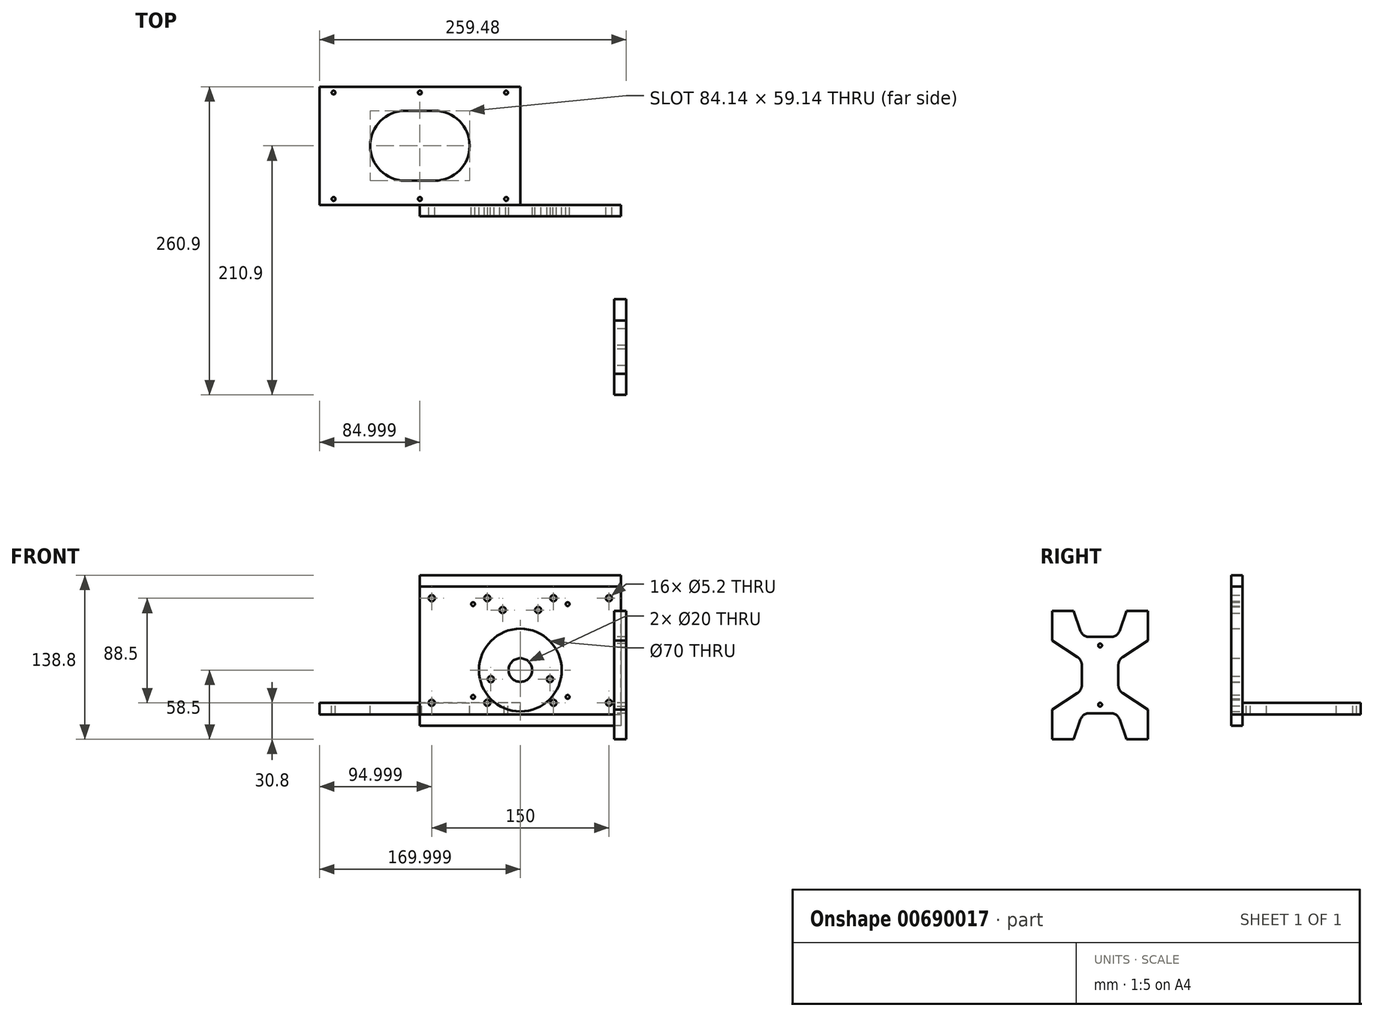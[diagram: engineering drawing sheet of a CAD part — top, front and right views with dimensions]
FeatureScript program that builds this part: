
annotation { "Feature Type Name" : "Feature", "Feature Type Description" : "" }
export const myFeature = defineFeature(function(context is Context, id is Id, definition is map)
    precondition{}
    {
        {
            var Q0;
            Q0=qCreatedBy(makeId("Front.planeOp"),FACE);
            var sketch = newSketch(context, id + "F0", { "sketchPlane" : qUnion([Q0])});
            skLineSegment(sketch, "E0.bottom", {"start": v(-124.48, -10) * mm, "end": v(-34.48, -10) * mm});
            skLineSegment(sketch, "E0.top", {"start": v(-124.48, 98.5) * mm, "end": v(-34.48, 98.5) * mm});
            skLineSegment(sketch, "E0.left", {"start": v(-124.48, -10) * mm, "end": v(-124.48, 98.5) * mm});
            skLineSegment(sketch, "E0.right", {"start": v(-34.48, -10) * mm, "end": v(-34.48, 98.5) * mm});
            skLineSegment(sketch, "E1", {"start": v(-114.8, 27.7) * mm, "end": v(-55.3, 27.7) * mm, "construction": true});
            skCircle(sketch, "E2", {"center": v(-79.48, 27.7) * mm, "radius": 10 * mm});
            skLineSegment(sketch, "E3", {"start": v(-104.48, 103.79) * mm, "end": v(-104.48, -19.33) * mm, "construction": true});
            skLineSegment(sketch, "E4", {"start": v(-94.48, 107.47) * mm, "end": v(-94.48, -17.72) * mm, "construction": true});
            skLineSegment(sketch, "E5", {"start": v(-64.48, 105.92) * mm, "end": v(-64.48, -18.24) * mm, "construction": true});
            skLineSegment(sketch, "E6", {"start": v(-54.48, 104.54) * mm, "end": v(-54.48, -18.06) * mm, "construction": true});
            skLineSegment(sketch, "E7", {"start": v(-24.43, 78.5) * mm, "end": v(-130.75, 78.5) * mm, "construction": true});
            skLineSegment(sketch, "E8", {"start": v(-125.67, 20) * mm, "end": v(-19.96, 20) * mm, "construction": true});
            skCircle(sketch, "E9", {"center": v(-94.48, 78.5) * mm, "radius": 2.6 * mm});
            skCircle(sketch, "E10", {"center": v(-64.48, 78.5) * mm, "radius": 2.6 * mm});
            skCircle(sketch, "E11", {"center": v(-54.48, 20) * mm, "radius": 2.6 * mm});
            skCircle(sketch, "E12", {"center": v(-104.48, 20) * mm, "radius": 2.6 * mm});
            skCircle(sketch, "E13", {"center": v(-79.48, 27.7) * mm, "radius": 35 * mm});
            skLineSegment(sketch, "E14.bottom", {"start": v(-124.48, -10) * mm, "end": v(-164.48, -10) * mm});
            skLineSegment(sketch, "E14.top", {"start": v(-124.48, 98.5) * mm, "end": v(-164.48, 98.5) * mm});
            skLineSegment(sketch, "E14.right", {"start": v(-164.48, -10) * mm, "end": v(-164.48, 98.5) * mm});
            skLineSegment(sketch, "E15.bottom", {"start": v(-34.48, -10) * mm, "end": v(5.52, -10) * mm});
            skLineSegment(sketch, "E15.top", {"start": v(-34.48, 98.5) * mm, "end": v(5.52, 98.5) * mm});
            skLineSegment(sketch, "E15.right", {"start": v(5.52, -10) * mm, "end": v(5.52, 98.5) * mm});
            skCircle(sketch, "E16", {"center": v(-107.48, 0) * mm, "radius": 2.6 * mm});
            skCircle(sketch, "E17", {"center": v(-51.48, 0) * mm, "radius": 2.6 * mm});
            skCircle(sketch, "E18", {"center": v(-51.48, 88.5) * mm, "radius": 2.6 * mm});
            skCircle(sketch, "E19", {"center": v(-107.48, 88.5) * mm, "radius": 2.6 * mm});
            skLineSegment(sketch, "E20", {"start": v(-191.34, 0) * mm, "end": v(90.56, 0) * mm, "construction": true});
            skLineSegment(sketch, "E21", {"start": v(-191.67, 88.5) * mm, "end": v(79.33, 88.5) * mm, "construction": true});
            skLineSegment(sketch, "E22", {"start": v(-107.48, -48.79) * mm, "end": v(-107.48, 164.35) * mm, "construction": true});
            skLineSegment(sketch, "E23", {"start": v(-51.48, -54.74) * mm, "end": v(-51.48, 152.44) * mm, "construction": true});
            skCircle(sketch, "E24", {"center": v(-154.44, 88.5) * mm, "radius": 2.6 * mm});
            skCircle(sketch, "E25", {"center": v(-4.48, 88.5) * mm, "radius": 2.6 * mm});
            skCircle(sketch, "E26", {"center": v(-4.48, 0) * mm, "radius": 2.6 * mm});
            skLineSegment(sketch, "E27", {"start": v(-4.48, 123.23) * mm, "end": v(-4.48, -81.76) * mm, "construction": true});
            skLineSegment(sketch, "E28", {"start": v(-154.48, 116.5) * mm, "end": v(-154.48, -51.97) * mm, "construction": true});
            skCircle(sketch, "E29", {"center": v(-154.48, 0) * mm, "radius": 2.6 * mm});
            skLineSegment(sketch, "E30", {"start": v(-119.48, 133.53) * mm, "end": v(-119.48, -72.31) * mm, "construction": true});
            skLineSegment(sketch, "E31", {"start": v(-39.48, 143.72) * mm, "end": v(-39.48, -75.85) * mm, "construction": true});
            skLineSegment(sketch, "E32", {"start": v(-190.12, 83.5) * mm, "end": v(57.15, 83.5) * mm, "construction": true});
            skLineSegment(sketch, "E33", {"start": v(-180.8, 5) * mm, "end": v(49.63, 5) * mm, "construction": true});
            skCircle(sketch, "E34", {"center": v(-119.48, 83.5) * mm, "radius": 1.6 * mm});
            skCircle(sketch, "E35", {"center": v(-39.48, 83.5) * mm, "radius": 1.6 * mm});
            skCircle(sketch, "E36", {"center": v(-39.48, 5) * mm, "radius": 1.6 * mm});
            skCircle(sketch, "E37", {"center": v(-119.48, 5) * mm, "radius": 1.6 * mm});
            skLineSegment(sketch, "E38", {"start": v(5.52, 98.5) * mm, "end": v(5.52, 108) * mm});
            skLineSegment(sketch, "E39", {"start": v(5.52, 108) * mm, "end": v(-164.48, 108) * mm});
            skLineSegment(sketch, "E40", {"start": v(-164.48, 108) * mm, "end": v(-164.48, 98.5) * mm});
            skLineSegment(sketch, "E41", {"start": v(5.52, -10) * mm, "end": v(5.52, -19.5) * mm});
            skLineSegment(sketch, "E42", {"start": v(5.52, -19.5) * mm, "end": v(-164.48, -19.5) * mm});
            skLineSegment(sketch, "E43", {"start": v(-164.48, -19.5) * mm, "end": v(-164.48, -10) * mm});
            skSolve(sketch);
        }
        {
            var Q0;
            Q0=makeQuery(id+"F0.imprint","IMPRINT",FACE,{"disambiguationData":[TD([[makeQuery(id+"F0.imprint","IMPRINT",EDGE,{"derivedFrom":sQuery(id+"F0.wireOp",EDGE,"E0.bottom")}),1.0]])]});
            var Q1;
            Q1=makeQuery(id+"F0.imprint","IMPRINT",FACE,{"disambiguationData":[TD([[makeQuery(id+"F0.imprint","IMPRINT",EDGE,{"derivedFrom":sQuery(id+"F0.wireOp",EDGE,"E2")}),-1.0]])]});
            var Q2;
            Q2=makeQuery(id+"F0.imprint","IMPRINT",FACE,{"disambiguationData":[TD([[makeQuery(id+"F0.imprint","IMPRINT",EDGE,{"derivedFrom":sQuery(id+"F0.wireOp",EDGE,"E14.bottom")}),-1.0]])]});
            var Q3;
            Q3=makeQuery(id+"F0.imprint","IMPRINT",FACE,{"disambiguationData":[TD([[makeQuery(id+"F0.imprint","IMPRINT",EDGE,{"derivedFrom":sQuery(id+"F0.wireOp",EDGE,"E15.bottom")}),1.0]])]});
            extrude(context, id + "F1", {"entities" : qUnion([Q0, Q1, Q2, Q3]), "depth" : 9.5 * mm, "offsetDistance" : 25 * mm});
        }
        {
            var Q0;
            Q0=qCreatedBy(makeId("Top.planeOp"),FACE);
            var sketch = newSketch(context, id + "F2", { "sketchPlane" : qUnion([Q0])});
            skLineSegment(sketch, "E44.bottom", {"start": v(-79.48, 0) * mm, "end": v(-249.48, 0) * mm});
            skLineSegment(sketch, "E44.top", {"start": v(-79.48, 100) * mm, "end": v(-249.48, 100) * mm});
            skLineSegment(sketch, "E44.left", {"start": v(-249.48, 0) * mm, "end": v(-249.48, 100) * mm});
            skLineSegment(sketch, "E44.right", {"start": v(-79.48, 0) * mm, "end": v(-79.48, 100) * mm});
            skLineSegment(sketch, "E45", {"start": v(-46.07, 5) * mm, "end": v(-297.56, 5) * mm, "construction": true});
            skLineSegment(sketch, "E46", {"start": v(-50, 95) * mm, "end": v(-298.28, 95) * mm, "construction": true});
            skLineSegment(sketch, "E47", {"start": v(-237.48, -41.3) * mm, "end": v(-237.48, 128.64) * mm, "construction": true});
            skLineSegment(sketch, "E48", {"start": v(-91.48, -65.97) * mm, "end": v(-91.48, 125.77) * mm, "construction": true});
            skLineSegment(sketch, "E49", {"start": v(-164.48, -45.87) * mm, "end": v(-164.48, 126.91) * mm, "construction": true});
            skPoint(sketch, "E49.startSnap0", {"position": v(-164.48, 0) * mm});
            skPoint(sketch, "E49.endSnap0", {"position": v(-164.48, 100) * mm});
            skCircle(sketch, "E50", {"center": v(-91.48, 5) * mm, "radius": 1.6 * mm});
            skCircle(sketch, "E51", {"center": v(-91.48, 95) * mm, "radius": 1.6 * mm});
            skCircle(sketch, "E52", {"center": v(-164.48, 5) * mm, "radius": 1.6 * mm});
            skCircle(sketch, "E53", {"center": v(-237.48, 5) * mm, "radius": 1.6 * mm});
            skCircle(sketch, "E54", {"center": v(-237.48, 95) * mm, "radius": 1.6 * mm});
            skCircle(sketch, "E55", {"center": v(-164.48, 95) * mm, "radius": 1.6 * mm});
            skLineSegment(sketch, "E56", {"start": v(-260.96, 50) * mm, "end": v(-20.94, 50) * mm, "construction": true});
            skPoint(sketch, "E56.startSnap0", {"position": v(-249.48, 50) * mm});
            skLineSegment(sketch, "E57", {"start": v(-176.98, 20.43) * mm, "end": v(-151.98, 20.43) * mm});
            skLineSegment(sketch, "E58", {"start": v(-176.98, 79.57) * mm, "end": v(-151.98, 79.57) * mm});
            skArc(sketch, "E59", {"start": v(-176.98, 20.43) * mm, "mid": v(-206.55, 50) * mm, "end": v(-176.98, 79.57) * mm});
            skArc(sketch, "E60", {"start": v(-151.98, 20.43) * mm, "mid": v(-122.41, 50) * mm, "end": v(-151.98, 79.57) * mm});
            skCircle(sketch, "E61", {"center": v(-176.98, 50) * mm, "radius": 1.6 * mm});
            skCircle(sketch, "E62", {"center": v(-151.98, 50) * mm, "radius": 1.6 * mm});
            skSolve(sketch);
        }
        {
            var Q0;
            Q0 = qSketchRegion(id + "F2", true);
            extrude(context, id + "F3", {"entities" : qUnion([Q0]), "oppositeDirection" : true, "depth" : 10 * mm, "offsetDistance" : 25 * mm});
        }
        {
            var Q0;
            Q0=qCreatedBy(makeId("Right.planeOp"),FACE);
            var sketch = newSketch(context, id + "F4", { "sketchPlane" : qUnion([Q0])});
            skLineSegment(sketch, "E63.bottom", {"start": v(-160.9, 77.7) * mm, "end": v(-79.9, 77.7) * mm});
            skLineSegment(sketch, "E63.top", {"start": v(-160.9, -30.8) * mm, "end": v(-79.9, -30.8) * mm});
            skLineSegment(sketch, "E63.left", {"start": v(-160.9, 77.7) * mm, "end": v(-160.9, -30.8) * mm});
            skLineSegment(sketch, "E63.right", {"start": v(-79.9, 77.7) * mm, "end": v(-79.9, -30.8) * mm});
            skLineSegment(sketch, "E64", {"start": v(-180.8, 23.45) * mm, "end": v(-56.26, 23.45) * mm, "construction": true});
            skPoint(sketch, "E64.startSnap0", {"position": v(-160.9, 23.45) * mm});
            skLineSegment(sketch, "E65", {"start": v(-120.4, 89.62) * mm, "end": v(-120.4, -39.77) * mm, "construction": true});
            skPoint(sketch, "E65.startSnap0", {"position": v(-120.4, 77.7) * mm});
            skLineSegment(sketch, "E66", {"start": v(-104.9, 14.85) * mm, "end": v(-104.9, 32.05) * mm});
            skLineSegment(sketch, "E67", {"start": v(-142.9, 77.7) * mm, "end": v(-137, 61.03) * mm});
            skLineSegment(sketch, "E68", {"start": v(-129.46, 55.7) * mm, "end": v(-111.34, 55.7) * mm});
            skLineSegment(sketch, "E69", {"start": v(-103.8, 61.03) * mm, "end": v(-97.9, 77.7) * mm});
            skLineSegment(sketch, "E70", {"start": v(-142.9, -30.8) * mm, "end": v(-137, -14.13) * mm});
            skLineSegment(sketch, "E71", {"start": v(-129.46, -8.8) * mm, "end": v(-111.34, -8.8) * mm});
            skLineSegment(sketch, "E72", {"start": v(-103.8, -14.13) * mm, "end": v(-97.9, -30.8) * mm});
            skLineSegment(sketch, "E73", {"start": v(-139.53, 38.75) * mm, "end": v(-160.9, 52.7) * mm});
            skLineSegment(sketch, "E74", {"start": v(-101.27, 38.75) * mm, "end": v(-79.9, 52.7) * mm});
            skLineSegment(sketch, "E75", {"start": v(-135.9, 32.05) * mm, "end": v(-135.9, 14.85) * mm});
            skLineSegment(sketch, "E76", {"start": v(-139.53, 8.15) * mm, "end": v(-160.9, -5.8) * mm});
            skLineSegment(sketch, "E77", {"start": v(-101.27, 8.15) * mm, "end": v(-79.9, -5.8) * mm});
            skPoint(sketch, "E78.visualSharp", {"position": v(-104.9, 36.39) * mm});
            skArc(sketch, "E78.filletArc", {"start": v(-101.27, 38.75) * mm, "mid": v(-103.94, 35.86) * mm, "end": v(-104.9, 32.05) * mm});
            skPoint(sketch, "E79.visualSharp", {"position": v(-104.9, 10.52) * mm});
            skArc(sketch, "E79.filletArc", {"start": v(-104.9, 14.85) * mm, "mid": v(-103.94, 11.04) * mm, "end": v(-101.27, 8.15) * mm});
            skPoint(sketch, "E80.visualSharp", {"position": v(-135.9, 10.52) * mm});
            skArc(sketch, "E80.filletArc", {"start": v(-139.53, 8.15) * mm, "mid": v(-136.87, 11.04) * mm, "end": v(-135.9, 14.85) * mm});
            skPoint(sketch, "E81.visualSharp", {"position": v(-135.9, 36.39) * mm});
            skArc(sketch, "E81.filletArc", {"start": v(-135.9, 32.05) * mm, "mid": v(-136.87, 35.86) * mm, "end": v(-139.53, 38.75) * mm});
            skPoint(sketch, "E82.visualSharp", {"position": v(-135.11, 55.7) * mm});
            skArc(sketch, "E82.filletArc", {"start": v(-137, 61.03) * mm, "mid": v(-134.08, 57.17) * mm, "end": v(-129.46, 55.7) * mm});
            skPoint(sketch, "E83.visualSharp", {"position": v(-105.7, 55.7) * mm});
            skArc(sketch, "E83.filletArc", {"start": v(-111.34, 55.7) * mm, "mid": v(-106.73, 57.17) * mm, "end": v(-103.8, 61.03) * mm});
            skPoint(sketch, "E84.visualSharp", {"position": v(-105.7, -8.8) * mm});
            skArc(sketch, "E84.filletArc", {"start": v(-103.8, -14.13) * mm, "mid": v(-106.73, -10.26) * mm, "end": v(-111.34, -8.8) * mm});
            skPoint(sketch, "E85.visualSharp", {"position": v(-135.11, -8.8) * mm});
            skArc(sketch, "E85.filletArc", {"start": v(-129.46, -8.8) * mm, "mid": v(-134.08, -10.26) * mm, "end": v(-137, -14.13) * mm});
            skCircle(sketch, "E86", {"center": v(-120.4, 48.45) * mm, "radius": 1.6 * mm});
            skCircle(sketch, "E87", {"center": v(-120.4, -1.55) * mm, "radius": 1.6 * mm});
            skSolve(sketch);
        }
        {
            var Q0;
            {var subQ3=sQuery(id+"F4.wireOp",EDGE,"6BtBliIl-XIgv-ySIk-bRog-vjNOL9RD9Jmr.left");Q0=makeQuery(id+"F4.imprint","IMPRINT",FACE,{"disambiguationData":[TD([[makeQuery(id+"F4.imprint","IMPRINT",EDGE,{"derivedFrom":subQ3}),-1.0]])]});}
            var Q1;
            {var subQ4=sQuery(id+"F4.wireOp",EDGE,"UYvsb1t5-4bmk-JdHv-OzJk-y6f95GowE9Ny");Q1=makeQuery(id+"F4.imprint","IMPRINT",FACE,{"disambiguationData":[TD([[makeQuery(id+"F4.imprint","IMPRINT",EDGE,{"derivedFrom":subQ4}),1.0]])]});}
            var Q2;
            Q2=makeQuery(id+"F4.imprint","IMPRINT",FACE,{"disambiguationData":[TD([[makeQuery(id+"F4.imprint","IMPRINT",EDGE,{"derivedFrom":sQuery(id+"F4.wireOp",EDGE,"E63.bottom")}),-1.0]])]});
            extrude(context, id + "F5", {"entities" : qUnion([Q0, Q1, Q2]), "depth" : 10 * mm, "offsetDistance" : 25 * mm});
        }
        {
            var Q0;
            Q0=makeQuery(id+"F0.imprint","IMPRINT",FACE,{"disambiguationData":[TD([[makeQuery(id+"F0.imprint","IMPRINT",EDGE,{"derivedFrom":sQuery(id+"F0.wireOp",EDGE,"E0.bottom")}),1.0]])]});
            var Q1;
            Q1=makeQuery(id+"F0.imprint","IMPRINT",FACE,{"disambiguationData":[TD([[makeQuery(id+"F0.imprint","IMPRINT",EDGE,{"derivedFrom":sQuery(id+"F0.wireOp",EDGE,"E17")}),1.0]])]});
            var Q2;
            Q2=makeQuery(id+"F0.imprint","IMPRINT",FACE,{"disambiguationData":[TD([[makeQuery(id+"F0.imprint","IMPRINT",EDGE,{"derivedFrom":sQuery(id+"F0.wireOp",EDGE,"E15.bottom")}),1.0]])]});
            var Q3;
            Q3=makeQuery(id+"F0.imprint","IMPRINT",FACE,{"disambiguationData":[TD([[makeQuery(id+"F0.imprint","IMPRINT",EDGE,{"derivedFrom":sQuery(id+"F0.wireOp",EDGE,"E16")}),1.0]])]});
            var Q4;
            Q4=makeQuery(id+"F0.imprint","IMPRINT",FACE,{"disambiguationData":[TD([[makeQuery(id+"F0.imprint","IMPRINT",EDGE,{"derivedFrom":sQuery(id+"F0.wireOp",EDGE,"E9")}),1.0]])]});
            var Q5;
            Q5=makeQuery(id+"F0.imprint","IMPRINT",FACE,{"disambiguationData":[TD([[makeQuery(id+"F0.imprint","IMPRINT",EDGE,{"derivedFrom":sQuery(id+"F0.wireOp",EDGE,"E10")}),1.0]])]});
            var Q6;
            Q6=makeQuery(id+"F0.imprint","IMPRINT",FACE,{"disambiguationData":[TD([[makeQuery(id+"F0.imprint","IMPRINT",EDGE,{"derivedFrom":sQuery(id+"F0.wireOp",EDGE,"E18")}),1.0]])]});
            var Q7;
            Q7=makeQuery(id+"F0.imprint","IMPRINT",FACE,{"disambiguationData":[TD([[makeQuery(id+"F0.imprint","IMPRINT",EDGE,{"derivedFrom":sQuery(id+"F0.wireOp",EDGE,"E19")}),1.0]])]});
            var Q8;
            Q8=makeQuery(id+"F0.imprint","IMPRINT",FACE,{"disambiguationData":[TD([[makeQuery(id+"F0.imprint","IMPRINT",EDGE,{"derivedFrom":sQuery(id+"F0.wireOp",EDGE,"E14.bottom")}),-1.0]])]});
            var Q9;
            Q9=makeQuery(id+"F0.imprint","IMPRINT",FACE,{"disambiguationData":[TD([[makeQuery(id+"F0.imprint","IMPRINT",EDGE,{"derivedFrom":sQuery(id+"F0.wireOp",EDGE,"E25")}),1.0]])]});
            var Q10;
            Q10=makeQuery(id+"F0.imprint","IMPRINT",FACE,{"disambiguationData":[TD([[makeQuery(id+"F0.imprint","IMPRINT",EDGE,{"derivedFrom":sQuery(id+"F0.wireOp",EDGE,"E26")}),1.0]])]});
            var Q11;
            Q11=makeQuery(id+"F0.imprint","IMPRINT",FACE,{"disambiguationData":[TD([[makeQuery(id+"F0.imprint","IMPRINT",EDGE,{"derivedFrom":sQuery(id+"F0.wireOp",EDGE,"E29")}),1.0]])]});
            var Q12;
            Q12=makeQuery(id+"F0.imprint","IMPRINT",FACE,{"disambiguationData":[TD([[makeQuery(id+"F0.imprint","IMPRINT",EDGE,{"derivedFrom":sQuery(id+"F0.wireOp",EDGE,"E24")}),1.0]])]});
            extrude(context, id + "F6", {"entities" : qUnion([Q0, Q1, Q2, Q3, Q4, Q5, Q6, Q7, Q8, Q9, Q10, Q11, Q12]), "depth" : 9.5 * mm, "offsetDistance" : 25 * mm});
        }
        {
            var Q0;
            Q0 = qSketchRegion(id + "F0", true);
            var Q1;
            Q1=makeQuery(id+"F0.imprint","IMPRINT",FACE,{"disambiguationData":[TD([[makeQuery(id+"F0.imprint","IMPRINT",EDGE,{"derivedFrom":sQuery(id+"F0.wireOp",EDGE,"E0.bottom")}),1.0]])]});
            var Q2;
            Q2=makeQuery(id+"F0.imprint","IMPRINT",FACE,{"disambiguationData":[TD([[makeQuery(id+"F0.imprint","IMPRINT",EDGE,{"derivedFrom":sQuery(id+"F0.wireOp",EDGE,"E2")}),-1.0]])]});
            var Q3;
            Q3=makeQuery(id+"F0.imprint","IMPRINT",FACE,{"disambiguationData":[TD([[makeQuery(id+"F0.imprint","IMPRINT",EDGE,{"derivedFrom":sQuery(id+"F0.wireOp",EDGE,"E17")}),1.0]])]});
            var Q4;
            Q4=makeQuery(id+"F0.imprint","IMPRINT",FACE,{"disambiguationData":[TD([[makeQuery(id+"F0.imprint","IMPRINT",EDGE,{"derivedFrom":sQuery(id+"F0.wireOp",EDGE,"E11")}),1.0]])]});
            var Q5;
            Q5=makeQuery(id+"F0.imprint","IMPRINT",FACE,{"disambiguationData":[TD([[makeQuery(id+"F0.imprint","IMPRINT",EDGE,{"derivedFrom":sQuery(id+"F0.wireOp",EDGE,"E12")}),1.0]])]});
            var Q6;
            Q6=makeQuery(id+"F0.imprint","IMPRINT",FACE,{"disambiguationData":[TD([[makeQuery(id+"F0.imprint","IMPRINT",EDGE,{"derivedFrom":sQuery(id+"F0.wireOp",EDGE,"E16")}),1.0]])]});
            var Q7;
            Q7=makeQuery(id+"F0.imprint","IMPRINT",FACE,{"disambiguationData":[TD([[makeQuery(id+"F0.imprint","IMPRINT",EDGE,{"derivedFrom":sQuery(id+"F0.wireOp",EDGE,"E37")}),1.0]])]});
            var Q8;
            Q8=makeQuery(id+"F0.imprint","IMPRINT",FACE,{"disambiguationData":[TD([[makeQuery(id+"F0.imprint","IMPRINT",EDGE,{"derivedFrom":sQuery(id+"F0.wireOp",EDGE,"E18")}),1.0]])]});
            var Q9;
            Q9=makeQuery(id+"F0.imprint","IMPRINT",FACE,{"disambiguationData":[TD([[makeQuery(id+"F0.imprint","IMPRINT",EDGE,{"derivedFrom":sQuery(id+"F0.wireOp",EDGE,"E10")}),1.0]])]});
            var Q10;
            Q10=makeQuery(id+"F0.imprint","IMPRINT",FACE,{"disambiguationData":[TD([[makeQuery(id+"F0.imprint","IMPRINT",EDGE,{"derivedFrom":sQuery(id+"F0.wireOp",EDGE,"E9")}),1.0]])]});
            var Q11;
            Q11=makeQuery(id+"F0.imprint","IMPRINT",FACE,{"disambiguationData":[TD([[makeQuery(id+"F0.imprint","IMPRINT",EDGE,{"derivedFrom":sQuery(id+"F0.wireOp",EDGE,"E19")}),1.0]])]});
            var Q12;
            Q12=makeQuery(id+"F0.imprint","IMPRINT",FACE,{"disambiguationData":[TD([[makeQuery(id+"F0.imprint","IMPRINT",EDGE,{"derivedFrom":sQuery(id+"F0.wireOp",EDGE,"E34")}),1.0]])]});
            var Q13;
            Q13=makeQuery(id+"F0.imprint","IMPRINT",FACE,{"disambiguationData":[TD([[makeQuery(id+"F0.imprint","IMPRINT",EDGE,{"derivedFrom":sQuery(id+"F0.wireOp",EDGE,"E35")}),1.0]])]});
            var Q14;
            Q14=makeQuery(id+"F0.imprint","IMPRINT",FACE,{"disambiguationData":[TD([[makeQuery(id+"F0.imprint","IMPRINT",EDGE,{"derivedFrom":sQuery(id+"F0.wireOp",EDGE,"E36")}),1.0]])]});
            extrude(context, id + "F7", {"entities" : qUnion([Q0, Q1, Q2, Q3, Q4, Q5, Q6, Q7, Q8, Q9, Q10, Q11, Q12, Q13, Q14]), "depth" : 9.5 * mm, "offsetDistance" : 25 * mm});
        }
    });
